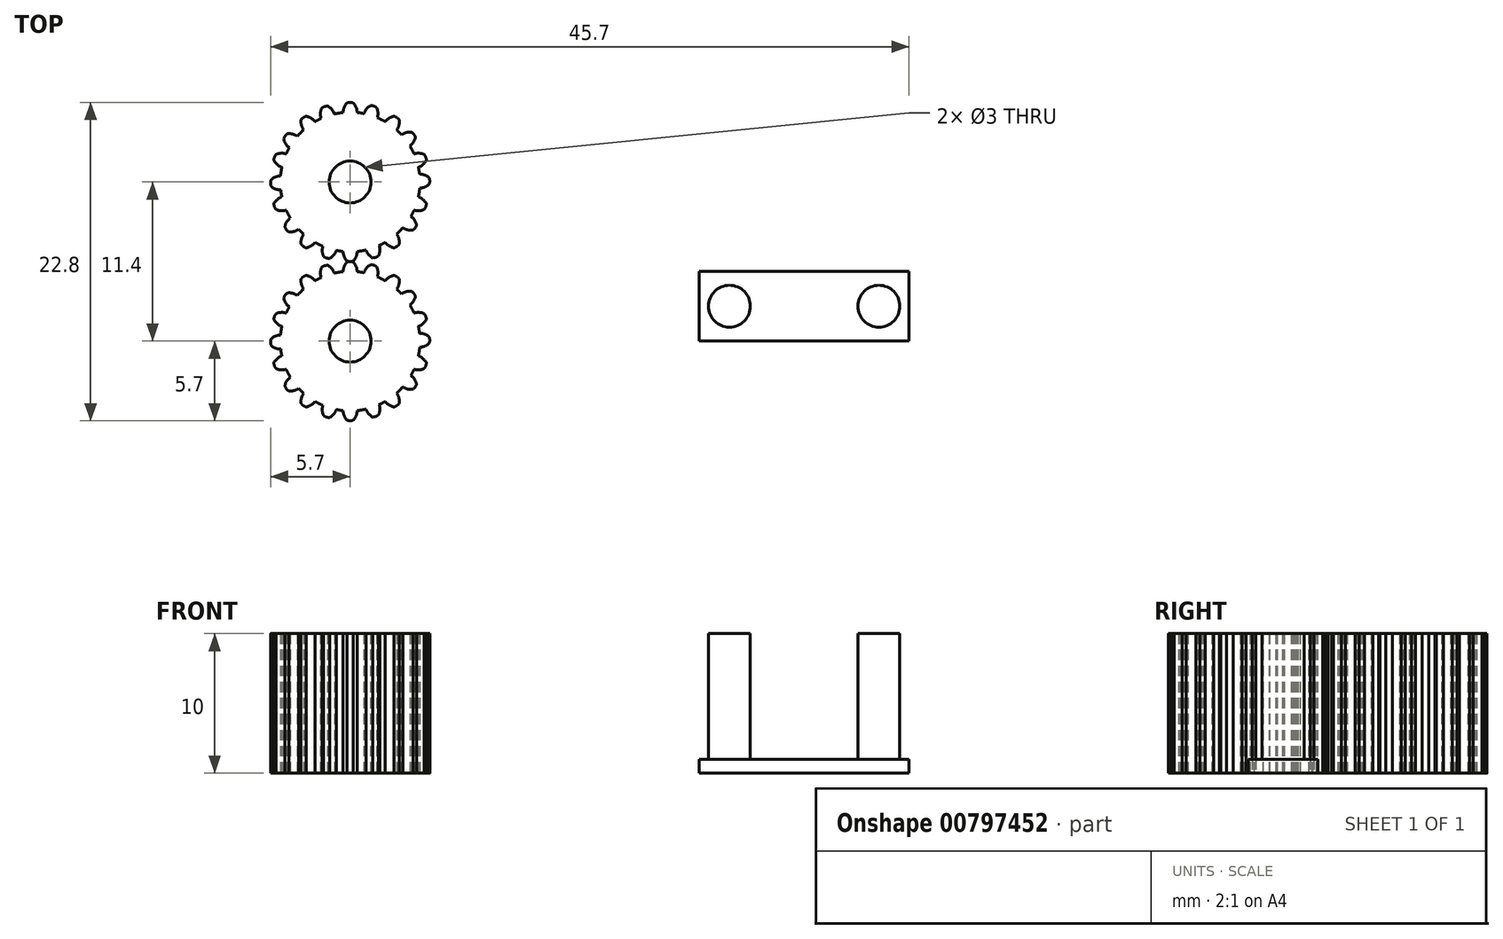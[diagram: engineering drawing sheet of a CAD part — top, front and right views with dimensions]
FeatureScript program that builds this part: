
annotation { "Feature Type Name" : "Feature", "Feature Type Description" : "" }
export const myFeature = defineFeature(function(context is Context, id is Id, definition is map)
    precondition{}
    {
        {
            var Q0;
            Q0=qCreatedBy(makeId("Top.planeOp"),FACE);
            var sketch = newSketch(context, id + "F0", { "sketchPlane" : qUnion([Q0])});
            skCircle(sketch, "E0", {"center": v(0, 0) * mm, "radius": 5 * mm});
            skCircle(sketch, "E1", {"center": v(0, 0) * mm, "radius": 1.5 * mm});
            skSolve(sketch);
        }
        {
            var Q0;
            Q0=qCreatedBy(makeId("Top.planeOp"),FACE);
            var sketch = newSketch(context, id + "F1", { "sketchPlane" : qUnion([Q0])});
            skArc(sketch, "E2", {"start": v(-0.5, 4.97) * mm, "mid": v(0, 5) * mm, "end": v(0.5, 4.97) * mm});
            skArc(sketch, "E3", {"start": v(0, 5) * mm, "mid": v(0.5, 4.97) * mm, "end": v(1, 4.9) * mm, "construction": true});
            skLineSegment(sketch, "E4", {"start": v(0, 5) * mm, "end": v(1, 4.9) * mm, "construction": true});
            skLineSegment(sketch, "E5", {"start": v(-0.5, 4.97) * mm, "end": v(0.5, 4.97) * mm, "construction": true});
            skArc(sketch, "E6", {"start": v(-0.5, 4.97) * mm, "mid": v(-0.43, 5.34) * mm, "end": v(-0.23, 5.66) * mm});
            skArc(sketch, "E7", {"start": v(0.5, 4.97) * mm, "mid": v(0.43, 5.34) * mm, "end": v(0.23, 5.66) * mm});
            skArc(sketch, "E8", {"start": v(-0.23, 5.66) * mm, "mid": v(0, 5.7) * mm, "end": v(0.23, 5.66) * mm});
            skLineSegment(sketch, "E9", {"start": v(0, 5.7) * mm, "end": v(0, 5) * mm, "construction": true});
            skArc(sketch, "E10", {"start": v(1, 4.9) * mm, "mid": v(1.48, 4.78) * mm, "end": v(1.95, 4.6) * mm});
            skLineSegment(sketch, "E11", {"start": v(1, 4.9) * mm, "end": v(1.95, 4.6) * mm, "construction": true});
            skLineSegment(sketch, "E12", {"start": v(0, 5) * mm, "end": v(1.48, 4.78) * mm, "construction": true});
            skArc(sketch, "E13", {"start": v(-1.72, 4.7) * mm, "mid": v(2.8, 4.14) * mm, "end": v(5, 0.15) * mm, "construction": true});
            skLineSegment(sketch, "E14", {"start": v(0, 0) * mm, "end": v(1.7, 5.44) * mm, "construction": true});
            skArc(sketch, "E15", {"start": v(1, 4.9) * mm, "mid": v(1.17, 5.23) * mm, "end": v(1.46, 5.47) * mm});
            skArc(sketch, "E16", {"start": v(1.95, 4.6) * mm, "mid": v(2, 4.98) * mm, "end": v(1.9, 5.34) * mm});
            skArc(sketch, "E17", {"start": v(1.46, 5.47) * mm, "mid": v(1.69, 5.45) * mm, "end": v(1.9, 5.34) * mm});
            skArc(sketch, "E18.1.0", {"start": v(3.69, 3.38) * mm, "mid": v(4, 3) * mm, "end": v(4.28, 2.58) * mm});
            skArc(sketch, "E18.1.1", {"start": v(2.52, 4.32) * mm, "mid": v(2.8, 4.58) * mm, "end": v(3.15, 4.71) * mm});
            skArc(sketch, "E18.1.2", {"start": v(3.69, 3.38) * mm, "mid": v(4.02, 3.54) * mm, "end": v(4.4, 3.57) * mm});
            skLineSegment(sketch, "E18.1.3", {"start": v(3.35, 4.61) * mm, "end": v(2.94, 4.05) * mm, "construction": true});
            skLineSegment(sketch, "E18.1.4", {"start": v(2.94, 4.05) * mm, "end": v(4, 3) * mm, "construction": true});
            skLineSegment(sketch, "E18.1.5", {"start": v(2.52, 4.32) * mm, "end": v(3.33, 3.73) * mm, "construction": true});
            skArc(sketch, "E18.1.6", {"start": v(4.28, 2.58) * mm, "mid": v(4.54, 2.86) * mm, "end": v(4.67, 3.21) * mm});
            skArc(sketch, "E18.1.7", {"start": v(3.33, 3.73) * mm, "mid": v(3.49, 4.07) * mm, "end": v(3.51, 4.45) * mm});
            skArc(sketch, "E18.1.8", {"start": v(2.52, 4.32) * mm, "mid": v(2.94, 4.05) * mm, "end": v(3.33, 3.73) * mm});
            skLineSegment(sketch, "E18.1.9", {"start": v(3.69, 3.38) * mm, "end": v(4.28, 2.58) * mm, "construction": true});
            skLineSegment(sketch, "E18.1.10", {"start": v(2.94, 4.05) * mm, "end": v(3.69, 3.38) * mm, "construction": true});
            skArc(sketch, "E18.1.11", {"start": v(3.15, 4.71) * mm, "mid": v(3.35, 4.61) * mm, "end": v(3.51, 4.45) * mm});
            skArc(sketch, "E18.1.12", {"start": v(2.94, 4.05) * mm, "mid": v(3.33, 3.73) * mm, "end": v(3.69, 3.38) * mm, "construction": true});
            skArc(sketch, "E18.1.13", {"start": v(4.4, 3.57) * mm, "mid": v(4.56, 3.41) * mm, "end": v(4.67, 3.21) * mm});
            skArc(sketch, "E18.2.0", {"start": v(4.97, 0.57) * mm, "mid": v(5, 0.07) * mm, "end": v(4.98, -0.43) * mm});
            skArc(sketch, "E18.2.1", {"start": v(4.58, 2.01) * mm, "mid": v(4.95, 2.06) * mm, "end": v(5.32, 1.96) * mm});
            skArc(sketch, "E18.2.2", {"start": v(4.97, 0.57) * mm, "mid": v(5.34, 0.5) * mm, "end": v(5.66, 0.3) * mm});
            skLineSegment(sketch, "E18.2.3", {"start": v(5.42, 1.76) * mm, "end": v(4.76, 1.55) * mm, "construction": true});
            skLineSegment(sketch, "E18.2.4", {"start": v(4.76, 1.55) * mm, "end": v(5, 0.07) * mm, "construction": true});
            skLineSegment(sketch, "E18.2.5", {"start": v(4.58, 2.01) * mm, "end": v(4.89, 1.06) * mm, "construction": true});
            skArc(sketch, "E18.2.6", {"start": v(4.98, -0.43) * mm, "mid": v(5.35, -0.36) * mm, "end": v(5.67, -0.15) * mm});
            skArc(sketch, "E18.2.7", {"start": v(4.89, 1.06) * mm, "mid": v(5.22, 1.24) * mm, "end": v(5.46, 1.53) * mm});
            skArc(sketch, "E18.2.8", {"start": v(4.58, 2.01) * mm, "mid": v(4.76, 1.55) * mm, "end": v(4.89, 1.06) * mm});
            skLineSegment(sketch, "E18.2.9", {"start": v(4.97, 0.57) * mm, "end": v(4.98, -0.43) * mm, "construction": true});
            skLineSegment(sketch, "E18.2.10", {"start": v(4.76, 1.55) * mm, "end": v(4.97, 0.57) * mm, "construction": true});
            skArc(sketch, "E18.2.11", {"start": v(5.32, 1.96) * mm, "mid": v(5.42, 1.76) * mm, "end": v(5.46, 1.53) * mm});
            skArc(sketch, "E18.2.12", {"start": v(4.76, 1.55) * mm, "mid": v(4.89, 1.06) * mm, "end": v(4.97, 0.57) * mm, "construction": true});
            skArc(sketch, "E18.2.13", {"start": v(5.66, 0.3) * mm, "mid": v(5.7, 0.08) * mm, "end": v(5.67, -0.15) * mm});
            skArc(sketch, "E18.3.0", {"start": v(4.35, -2.46) * mm, "mid": v(4.08, -2.88) * mm, "end": v(3.78, -3.28) * mm});
            skArc(sketch, "E18.3.1", {"start": v(4.89, -1.06) * mm, "mid": v(5.22, -1.24) * mm, "end": v(5.46, -1.53) * mm});
            skArc(sketch, "E18.3.2", {"start": v(4.35, -2.46) * mm, "mid": v(4.61, -2.73) * mm, "end": v(4.76, -3.08) * mm});
            skLineSegment(sketch, "E18.3.3", {"start": v(5.42, -1.76) * mm, "end": v(4.76, -1.55) * mm, "construction": true});
            skLineSegment(sketch, "E18.3.4", {"start": v(4.76, -1.55) * mm, "end": v(4.08, -2.89) * mm, "construction": true});
            skLineSegment(sketch, "E18.3.5", {"start": v(4.89, -1.06) * mm, "end": v(4.58, -2.01) * mm, "construction": true});
            skArc(sketch, "E18.3.6", {"start": v(3.78, -3.28) * mm, "mid": v(4.12, -3.43) * mm, "end": v(4.5, -3.45) * mm});
            skArc(sketch, "E18.3.7", {"start": v(4.58, -2.01) * mm, "mid": v(4.95, -2.06) * mm, "end": v(5.32, -1.96) * mm});
            skArc(sketch, "E18.3.8", {"start": v(4.89, -1.06) * mm, "mid": v(4.76, -1.55) * mm, "end": v(4.58, -2.01) * mm});
            skLineSegment(sketch, "E18.3.9", {"start": v(4.35, -2.46) * mm, "end": v(3.78, -3.28) * mm, "construction": true});
            skLineSegment(sketch, "E18.3.10", {"start": v(4.76, -1.55) * mm, "end": v(4.35, -2.46) * mm, "construction": true});
            skArc(sketch, "E18.3.11", {"start": v(5.46, -1.53) * mm, "mid": v(5.42, -1.76) * mm, "end": v(5.32, -1.96) * mm});
            skArc(sketch, "E18.3.12", {"start": v(4.76, -1.55) * mm, "mid": v(4.58, -2.01) * mm, "end": v(4.35, -2.46) * mm, "construction": true});
            skArc(sketch, "E18.3.13", {"start": v(4.76, -3.08) * mm, "mid": v(4.66, -3.29) * mm, "end": v(4.5, -3.45) * mm});
            skArc(sketch, "E18.4.0", {"start": v(2.08, -4.55) * mm, "mid": v(1.6, -4.73) * mm, "end": v(1.13, -4.87) * mm});
            skArc(sketch, "E18.4.1", {"start": v(3.33, -3.73) * mm, "mid": v(3.49, -4.07) * mm, "end": v(3.51, -4.45) * mm});
            skArc(sketch, "E18.4.2", {"start": v(2.08, -4.55) * mm, "mid": v(2.13, -4.92) * mm, "end": v(2.04, -5.29) * mm});
            skLineSegment(sketch, "E18.4.3", {"start": v(3.35, -4.61) * mm, "end": v(2.94, -4.05) * mm, "construction": true});
            skLineSegment(sketch, "E18.4.4", {"start": v(2.94, -4.05) * mm, "end": v(1.6, -4.73) * mm, "construction": true});
            skLineSegment(sketch, "E18.4.5", {"start": v(3.33, -3.73) * mm, "end": v(2.52, -4.32) * mm, "construction": true});
            skArc(sketch, "E18.4.6", {"start": v(1.13, -4.87) * mm, "mid": v(1.32, -5.2) * mm, "end": v(1.61, -5.43) * mm});
            skArc(sketch, "E18.4.7", {"start": v(2.52, -4.32) * mm, "mid": v(2.8, -4.58) * mm, "end": v(3.15, -4.71) * mm});
            skArc(sketch, "E18.4.8", {"start": v(3.33, -3.73) * mm, "mid": v(2.94, -4.05) * mm, "end": v(2.52, -4.32) * mm});
            skLineSegment(sketch, "E18.4.9", {"start": v(2.08, -4.55) * mm, "end": v(1.13, -4.87) * mm, "construction": true});
            skLineSegment(sketch, "E18.4.10", {"start": v(2.94, -4.05) * mm, "end": v(2.08, -4.55) * mm, "construction": true});
            skArc(sketch, "E18.4.11", {"start": v(3.51, -4.45) * mm, "mid": v(3.35, -4.61) * mm, "end": v(3.15, -4.71) * mm});
            skArc(sketch, "E18.4.12", {"start": v(2.94, -4.05) * mm, "mid": v(2.52, -4.32) * mm, "end": v(2.08, -4.55) * mm, "construction": true});
            skArc(sketch, "E18.4.13", {"start": v(2.04, -5.29) * mm, "mid": v(1.84, -5.4) * mm, "end": v(1.61, -5.43) * mm});
            skArc(sketch, "E18.5.0", {"start": v(-1, -4.9) * mm, "mid": v(-1.48, -4.78) * mm, "end": v(-1.95, -4.6) * mm});
            skArc(sketch, "E18.5.1", {"start": v(0.5, -4.97) * mm, "mid": v(0.43, -5.34) * mm, "end": v(0.23, -5.66) * mm});
            skArc(sketch, "E18.5.2", {"start": v(-1, -4.9) * mm, "mid": v(-1.17, -5.23) * mm, "end": v(-1.46, -5.47) * mm});
            skLineSegment(sketch, "E18.5.3", {"start": v(0, -5.7) * mm, "end": v(0, -5) * mm, "construction": true});
            skLineSegment(sketch, "E18.5.4", {"start": v(0, -5) * mm, "end": v(-1.48, -4.78) * mm, "construction": true});
            skLineSegment(sketch, "E18.5.5", {"start": v(0.5, -4.97) * mm, "end": v(-0.5, -4.97) * mm, "construction": true});
            skArc(sketch, "E18.5.6", {"start": v(-1.95, -4.6) * mm, "mid": v(-2, -4.98) * mm, "end": v(-1.9, -5.34) * mm});
            skArc(sketch, "E18.5.7", {"start": v(-0.5, -4.97) * mm, "mid": v(-0.43, -5.34) * mm, "end": v(-0.23, -5.66) * mm});
            skArc(sketch, "E18.5.8", {"start": v(0.5, -4.97) * mm, "mid": v(0, -5) * mm, "end": v(-0.5, -4.97) * mm});
            skLineSegment(sketch, "E18.5.9", {"start": v(-1, -4.9) * mm, "end": v(-1.95, -4.6) * mm, "construction": true});
            skLineSegment(sketch, "E18.5.10", {"start": v(0, -5) * mm, "end": v(-1, -4.9) * mm, "construction": true});
            skArc(sketch, "E18.5.11", {"start": v(0.23, -5.66) * mm, "mid": v(0, -5.7) * mm, "end": v(-0.23, -5.66) * mm});
            skArc(sketch, "E18.5.12", {"start": v(0, -5) * mm, "mid": v(-0.5, -4.97) * mm, "end": v(-1, -4.9) * mm, "construction": true});
            skArc(sketch, "E18.5.13", {"start": v(-1.46, -5.47) * mm, "mid": v(-1.69, -5.45) * mm, "end": v(-1.9, -5.34) * mm});
            skArc(sketch, "E18.6.0", {"start": v(-3.69, -3.38) * mm, "mid": v(-4, -3) * mm, "end": v(-4.28, -2.58) * mm});
            skArc(sketch, "E18.6.1", {"start": v(-2.52, -4.32) * mm, "mid": v(-2.8, -4.58) * mm, "end": v(-3.15, -4.71) * mm});
            skArc(sketch, "E18.6.2", {"start": v(-3.69, -3.38) * mm, "mid": v(-4.02, -3.54) * mm, "end": v(-4.4, -3.57) * mm});
            skLineSegment(sketch, "E18.6.3", {"start": v(-3.35, -4.61) * mm, "end": v(-2.94, -4.05) * mm, "construction": true});
            skLineSegment(sketch, "E18.6.4", {"start": v(-2.94, -4.05) * mm, "end": v(-4, -3) * mm, "construction": true});
            skLineSegment(sketch, "E18.6.5", {"start": v(-2.52, -4.32) * mm, "end": v(-3.33, -3.73) * mm, "construction": true});
            skArc(sketch, "E18.6.6", {"start": v(-4.28, -2.58) * mm, "mid": v(-4.54, -2.86) * mm, "end": v(-4.67, -3.21) * mm});
            skArc(sketch, "E18.6.7", {"start": v(-3.33, -3.73) * mm, "mid": v(-3.49, -4.07) * mm, "end": v(-3.51, -4.45) * mm});
            skArc(sketch, "E18.6.8", {"start": v(-2.52, -4.32) * mm, "mid": v(-2.94, -4.05) * mm, "end": v(-3.33, -3.73) * mm});
            skLineSegment(sketch, "E18.6.9", {"start": v(-3.69, -3.38) * mm, "end": v(-4.28, -2.58) * mm, "construction": true});
            skLineSegment(sketch, "E18.6.10", {"start": v(-2.94, -4.05) * mm, "end": v(-3.69, -3.38) * mm, "construction": true});
            skArc(sketch, "E18.6.11", {"start": v(-3.15, -4.71) * mm, "mid": v(-3.35, -4.61) * mm, "end": v(-3.51, -4.45) * mm});
            skArc(sketch, "E18.6.12", {"start": v(-2.94, -4.05) * mm, "mid": v(-3.33, -3.73) * mm, "end": v(-3.69, -3.38) * mm, "construction": true});
            skArc(sketch, "E18.6.13", {"start": v(-4.4, -3.57) * mm, "mid": v(-4.56, -3.41) * mm, "end": v(-4.67, -3.21) * mm});
            skArc(sketch, "E18.7.0", {"start": v(-4.97, -0.57) * mm, "mid": v(-5, -0.07) * mm, "end": v(-4.98, 0.43) * mm});
            skArc(sketch, "E18.7.1", {"start": v(-4.58, -2.01) * mm, "mid": v(-4.95, -2.06) * mm, "end": v(-5.32, -1.96) * mm});
            skArc(sketch, "E18.7.2", {"start": v(-4.97, -0.57) * mm, "mid": v(-5.34, -0.5) * mm, "end": v(-5.66, -0.3) * mm});
            skLineSegment(sketch, "E18.7.3", {"start": v(-5.42, -1.76) * mm, "end": v(-4.76, -1.55) * mm, "construction": true});
            skLineSegment(sketch, "E18.7.4", {"start": v(-4.76, -1.55) * mm, "end": v(-5, -0.07) * mm, "construction": true});
            skLineSegment(sketch, "E18.7.5", {"start": v(-4.58, -2.01) * mm, "end": v(-4.89, -1.06) * mm, "construction": true});
            skArc(sketch, "E18.7.6", {"start": v(-4.98, 0.43) * mm, "mid": v(-5.35, 0.36) * mm, "end": v(-5.67, 0.15) * mm});
            skArc(sketch, "E18.7.7", {"start": v(-4.89, -1.06) * mm, "mid": v(-5.22, -1.24) * mm, "end": v(-5.46, -1.53) * mm});
            skArc(sketch, "E18.7.8", {"start": v(-4.58, -2.01) * mm, "mid": v(-4.76, -1.55) * mm, "end": v(-4.89, -1.06) * mm});
            skLineSegment(sketch, "E18.7.9", {"start": v(-4.97, -0.57) * mm, "end": v(-4.98, 0.43) * mm, "construction": true});
            skLineSegment(sketch, "E18.7.10", {"start": v(-4.76, -1.55) * mm, "end": v(-4.97, -0.57) * mm, "construction": true});
            skArc(sketch, "E18.7.11", {"start": v(-5.32, -1.96) * mm, "mid": v(-5.42, -1.76) * mm, "end": v(-5.46, -1.53) * mm});
            skArc(sketch, "E18.7.12", {"start": v(-4.76, -1.55) * mm, "mid": v(-4.89, -1.06) * mm, "end": v(-4.97, -0.57) * mm, "construction": true});
            skArc(sketch, "E18.7.13", {"start": v(-5.66, -0.3) * mm, "mid": v(-5.7, -0.08) * mm, "end": v(-5.67, 0.15) * mm});
            skArc(sketch, "E18.8.0", {"start": v(-4.35, 2.46) * mm, "mid": v(-4.08, 2.88) * mm, "end": v(-3.78, 3.28) * mm});
            skArc(sketch, "E18.8.1", {"start": v(-4.89, 1.06) * mm, "mid": v(-5.22, 1.24) * mm, "end": v(-5.46, 1.53) * mm});
            skArc(sketch, "E18.8.2", {"start": v(-4.35, 2.46) * mm, "mid": v(-4.61, 2.73) * mm, "end": v(-4.76, 3.08) * mm});
            skLineSegment(sketch, "E18.8.3", {"start": v(-5.42, 1.76) * mm, "end": v(-4.76, 1.55) * mm, "construction": true});
            skLineSegment(sketch, "E18.8.4", {"start": v(-4.76, 1.55) * mm, "end": v(-4.08, 2.89) * mm, "construction": true});
            skLineSegment(sketch, "E18.8.5", {"start": v(-4.89, 1.06) * mm, "end": v(-4.58, 2.01) * mm, "construction": true});
            skArc(sketch, "E18.8.6", {"start": v(-3.78, 3.28) * mm, "mid": v(-4.12, 3.43) * mm, "end": v(-4.5, 3.45) * mm});
            skArc(sketch, "E18.8.7", {"start": v(-4.58, 2.01) * mm, "mid": v(-4.95, 2.06) * mm, "end": v(-5.32, 1.96) * mm});
            skArc(sketch, "E18.8.8", {"start": v(-4.89, 1.06) * mm, "mid": v(-4.76, 1.55) * mm, "end": v(-4.58, 2.01) * mm});
            skLineSegment(sketch, "E18.8.9", {"start": v(-4.35, 2.46) * mm, "end": v(-3.78, 3.28) * mm, "construction": true});
            skLineSegment(sketch, "E18.8.10", {"start": v(-4.76, 1.55) * mm, "end": v(-4.35, 2.46) * mm, "construction": true});
            skArc(sketch, "E18.8.11", {"start": v(-5.46, 1.53) * mm, "mid": v(-5.42, 1.76) * mm, "end": v(-5.32, 1.96) * mm});
            skArc(sketch, "E18.8.12", {"start": v(-4.76, 1.55) * mm, "mid": v(-4.58, 2.01) * mm, "end": v(-4.35, 2.46) * mm, "construction": true});
            skArc(sketch, "E18.8.13", {"start": v(-4.76, 3.08) * mm, "mid": v(-4.66, 3.29) * mm, "end": v(-4.5, 3.45) * mm});
            skArc(sketch, "E18.9.0", {"start": v(-2.08, 4.55) * mm, "mid": v(-1.6, 4.73) * mm, "end": v(-1.13, 4.87) * mm});
            skArc(sketch, "E18.9.1", {"start": v(-3.33, 3.73) * mm, "mid": v(-3.49, 4.07) * mm, "end": v(-3.51, 4.45) * mm});
            skArc(sketch, "E18.9.2", {"start": v(-2.08, 4.55) * mm, "mid": v(-2.13, 4.92) * mm, "end": v(-2.04, 5.29) * mm});
            skLineSegment(sketch, "E18.9.3", {"start": v(-3.35, 4.61) * mm, "end": v(-2.94, 4.05) * mm, "construction": true});
            skLineSegment(sketch, "E18.9.4", {"start": v(-2.94, 4.05) * mm, "end": v(-1.6, 4.73) * mm, "construction": true});
            skLineSegment(sketch, "E18.9.5", {"start": v(-3.33, 3.73) * mm, "end": v(-2.52, 4.32) * mm, "construction": true});
            skArc(sketch, "E18.9.6", {"start": v(-1.13, 4.87) * mm, "mid": v(-1.32, 5.2) * mm, "end": v(-1.61, 5.43) * mm});
            skArc(sketch, "E18.9.7", {"start": v(-2.52, 4.32) * mm, "mid": v(-2.8, 4.58) * mm, "end": v(-3.15, 4.71) * mm});
            skArc(sketch, "E18.9.8", {"start": v(-3.33, 3.73) * mm, "mid": v(-2.94, 4.05) * mm, "end": v(-2.52, 4.32) * mm});
            skLineSegment(sketch, "E18.9.9", {"start": v(-2.08, 4.55) * mm, "end": v(-1.13, 4.87) * mm, "construction": true});
            skLineSegment(sketch, "E18.9.10", {"start": v(-2.94, 4.05) * mm, "end": v(-2.08, 4.55) * mm, "construction": true});
            skArc(sketch, "E18.9.11", {"start": v(-3.51, 4.45) * mm, "mid": v(-3.35, 4.61) * mm, "end": v(-3.15, 4.71) * mm});
            skArc(sketch, "E18.9.12", {"start": v(-2.94, 4.05) * mm, "mid": v(-2.52, 4.32) * mm, "end": v(-2.08, 4.55) * mm, "construction": true});
            skArc(sketch, "E18.9.13", {"start": v(-2.04, 5.29) * mm, "mid": v(-1.84, 5.4) * mm, "end": v(-1.61, 5.43) * mm});
            skLineSegment(sketch, "E18.anchor1", {"start": v(0, 0) * mm, "end": v(-0.5, 4.97) * mm, "construction": true});
            skLineSegment(sketch, "E18.anchor2", {"start": v(0, 0) * mm, "end": v(-0.5, 4.97) * mm, "construction": true});
            skSolve(sketch);
        }
        {
            var Q0;
            Q0 = qSketchRegion(id + "F0", true);
            extrude(context, id + "F2", {"entities" : qUnion([Q0]), "depth" : 10 * mm, "offsetDistance" : 25 * mm});
        }
        {
            var Q0;
            Q0 = qSketchRegion(id + "F1", true);
            extrude(context, id + "F3", {"entities" : qUnion([Q0]), "operationType" : NewBodyOperationType.ADD, "depth" : 10 * mm, "offsetDistance" : 25 * mm});
        }
        {
            var Q0;
            Q0=makeQuery(id+"F2.opExtrude","SWEPT_BODY",BODY,{"disambiguationData":[OSD([sQuery(id+"F0.wireOp",EDGE,"E0")])]});
            transform(context, id + "F4", {"entities" : qUnion([Q0]), "transformType" : TransformType.TRANSLATION_3D, "dx" : 0 * mm, "dy" : 11.4 * mm, "dz" : 0 * mm, "makeCopy" : true});
        }
        {
            var Q0;
            Q0=qCreatedBy(makeId("Top.planeOp"),FACE);
            var sketch = newSketch(context, id + "F5", { "sketchPlane" : qUnion([Q0])});
            skLineSegment(sketch, "E19.bottom", {"start": v(25, 5) * mm, "end": v(40, 5) * mm});
            skLineSegment(sketch, "E19.top", {"start": v(25, 0) * mm, "end": v(40, 0) * mm});
            skLineSegment(sketch, "E19.left", {"start": v(25, 5) * mm, "end": v(25, 0) * mm});
            skLineSegment(sketch, "E19.right", {"start": v(40, 5) * mm, "end": v(40, 0) * mm});
            skLineSegment(sketch, "E20", {"start": v(25, 0) * mm, "end": v(0, 0) * mm, "construction": true});
            skSolve(sketch);
        }
        {
            var Q0;
            Q0 = qSketchRegion(id + "F5", true);
            extrude(context, id + "F6", {"entities" : qUnion([Q0]), "depth" : 1 * mm, "offsetDistance" : 25 * mm});
        }
        {
            var Q0;
            Q0=qCreatedBy(makeId("Top.planeOp"),FACE);
            var sketch = newSketch(context, id + "F7", { "sketchPlane" : qUnion([Q0])});
            skCircle(sketch, "E21", {"center": v(27.15, 2.5) * mm, "radius": 1.5 * mm});
            skCircle(sketch, "E22", {"center": v(37.85, 2.5) * mm, "radius": 1.5 * mm});
            skLineSegment(sketch, "E23", {"start": v(32.5, 0) * mm, "end": v(32.5, 5.76) * mm, "construction": true});
            skSolve(sketch);
        }
        {
            var Q0;
            Q0 = qSketchRegion(id + "F7", true);
            extrude(context, id + "F8", {"entities" : qUnion([Q0]), "operationType" : NewBodyOperationType.ADD, "depth" : 10 * mm, "offsetDistance" : 25 * mm});
        }
    });
